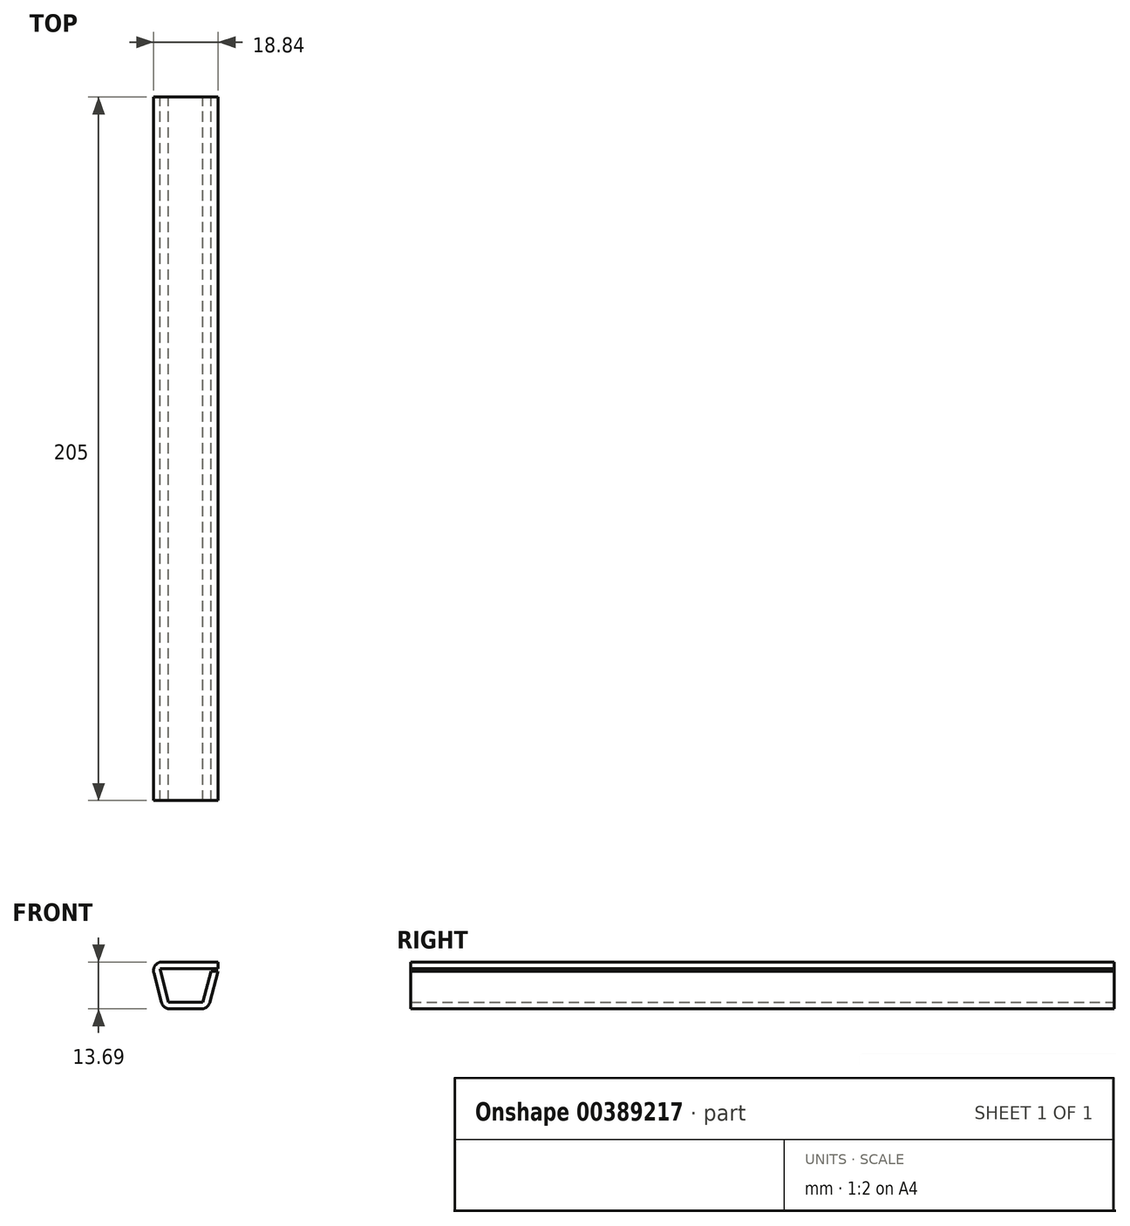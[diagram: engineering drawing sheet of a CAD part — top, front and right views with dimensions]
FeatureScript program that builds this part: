
annotation { "Feature Type Name" : "Feature", "Feature Type Description" : "" }
export const myFeature = defineFeature(function(context is Context, id is Id, definition is map)
    precondition{}
    {
        {
            var Q0;
            Q0=qCreatedBy(makeId("Front.planeOp"),FACE);
            var sketch = newSketch(context, id + "F0", { "sketchPlane" : qUnion([Q0])});
            skLineSegment(sketch, "E0", {"start": v(-6.5, -7.54) * mm, "end": v(3.5, -7.54) * mm});
            skLineSegment(sketch, "E1", {"start": v(3.5, -7.54) * mm, "end": v(-6.5, -7.54) * mm});
            skLineSegment(sketch, "E2", {"start": v(-6.5, -7.54) * mm, "end": v(-9, 2.15) * mm});
            skLineSegment(sketch, "E3", {"start": v(-9, 2.15) * mm, "end": v(8, 2.15) * mm});
            skLineSegment(sketch, "E4", {"start": v(3.5, -7.54) * mm, "end": v(5.93, 1.41) * mm});
            skLineSegment(sketch, "E5", {"start": v(5.93, 1.41) * mm, "end": v(8, 1.41) * mm});
            skLineSegment(sketch, "E6", {"start": v(8, 1.41) * mm, "end": v(5.54, -7.66) * mm});
            skLineSegment(sketch, "E7", {"start": v(3.09, -9.54) * mm, "end": v(-6.08, -9.54) * mm});
            skLineSegment(sketch, "E8", {"start": v(-8.54, -7.63) * mm, "end": v(-10.76, 0.97) * mm});
            skLineSegment(sketch, "E9", {"start": v(-8.3, 4.15) * mm, "end": v(8, 4.15) * mm});
            skLineSegment(sketch, "E10", {"start": v(8, 4.15) * mm, "end": v(8, 2.15) * mm});
            skPoint(sketch, "E11.visualSharp", {"position": v(5.03, -9.54) * mm});
            skArc(sketch, "E11.filletArc", {"start": v(3.09, -9.54) * mm, "mid": v(4.63, -9.01) * mm, "end": v(5.54, -7.66) * mm});
            skPoint(sketch, "E12.visualSharp", {"position": v(-8.05, -9.54) * mm});
            skArc(sketch, "E12.filletArc", {"start": v(-8.54, -7.63) * mm, "mid": v(-7.64, -9) * mm, "end": v(-6.08, -9.54) * mm});
            skPoint(sketch, "E13.visualSharp", {"position": v(-11.58, 4.15) * mm});
            skArc(sketch, "E13.filletArc", {"start": v(-8.3, 4.15) * mm, "mid": v(-10.31, 3.16) * mm, "end": v(-10.76, 0.97) * mm});
            skSolve(sketch);
        }
        {
            var Q0;
            Q0 = qSketchRegion(id + "F0", true);
            extrude(context, id + "F1", {"entities" : qUnion([Q0]), "depth" : 205 * mm, "offsetDistance" : 25.4 * mm});
        }
    });
